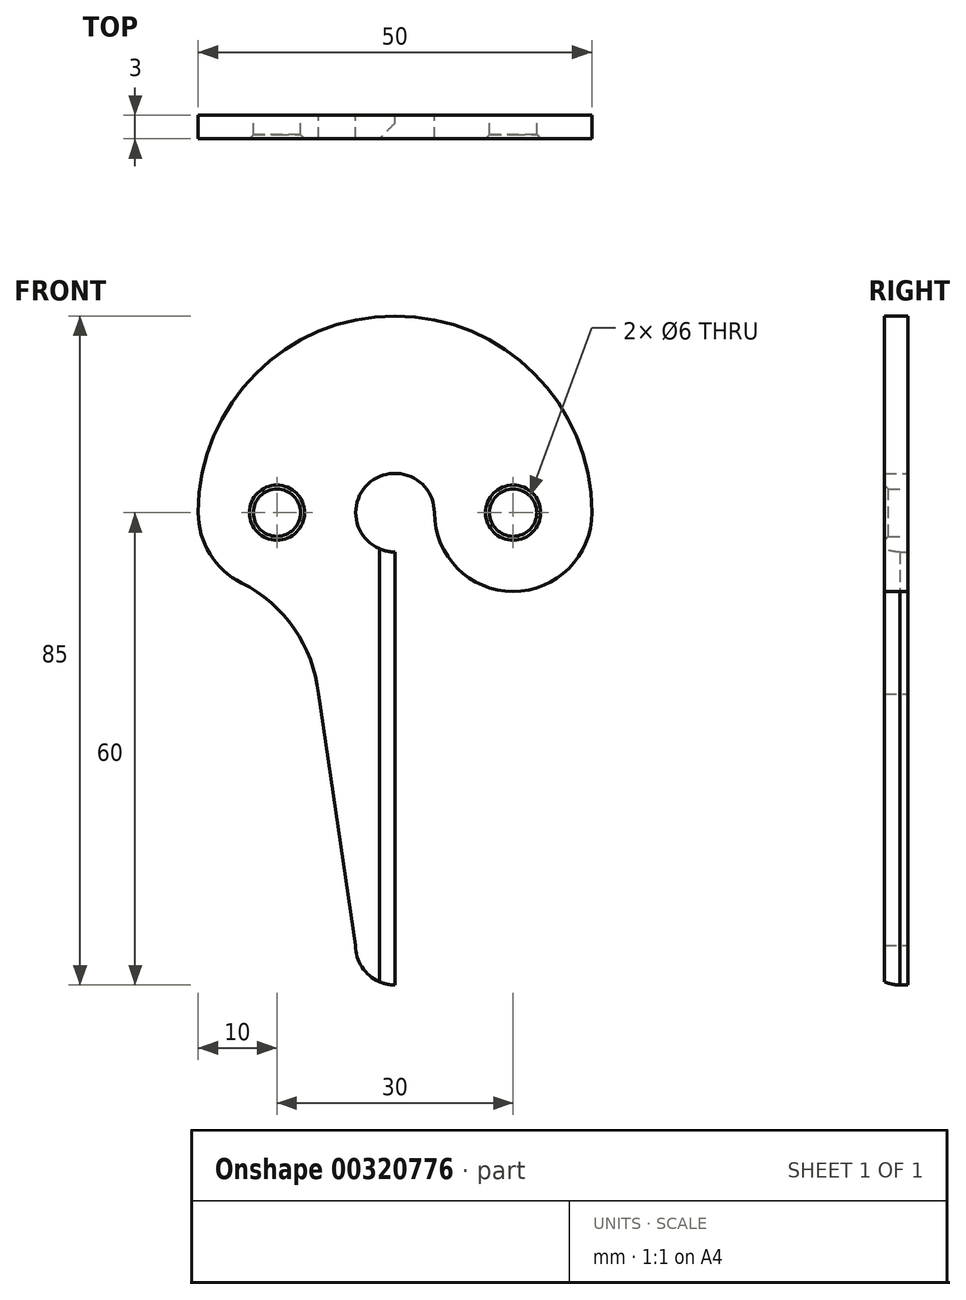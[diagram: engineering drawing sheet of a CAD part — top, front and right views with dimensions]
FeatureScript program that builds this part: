
annotation { "Feature Type Name" : "Feature", "Feature Type Description" : "" }
export const myFeature = defineFeature(function(context is Context, id is Id, definition is map)
    precondition{}
    {
        {
            var Q0;
            Q0=qCreatedBy(makeId("Front.planeOp"),FACE);
            var sketch = newSketch(context, id + "F0", { "sketchPlane" : qUnion([Q0])});
            skArc(sketch, "E0", {"start": v(25, 0) * mm, "mid": v(0, 25) * mm, "end": v(-25, 0) * mm});
            skArc(sketch, "E1", {"start": v(5, 0) * mm, "mid": v(-3.54, 3.54) * mm, "end": v(0, -5) * mm});
            skCircle(sketch, "E2", {"center": v(-15, 0) * mm, "radius": 3 * mm});
            skCircle(sketch, "E3", {"center": v(15, 0) * mm, "radius": 3 * mm});
            skCircle(sketch, "E4", {"center": v(-15, 0) * mm, "radius": 3.5 * mm});
            skCircle(sketch, "E5", {"center": v(15, 0) * mm, "radius": 3.5 * mm});
            skArc(sketch, "E6", {"start": v(-25, 0) * mm, "mid": v(-15, -10) * mm, "end": v(-5, 0) * mm});
            skArc(sketch, "E7", {"start": v(5, 0) * mm, "mid": v(15, -10) * mm, "end": v(25, 0) * mm});
            skPoint(sketch, "E8", {"position": v(-27.6, -25) * mm});
            skPoint(sketch, "E9", {"position": v(27.6, -25) * mm});
            skPoint(sketch, "E10", {"position": v(0, -54.97) * mm});
            skArc(sketch, "E11", {"start": v(-5.03, -54.97) * mm, "mid": v(-3.56, -58.53) * mm, "end": v(0, -60) * mm});
            skArc(sketch, "E12", {"start": v(-9.72, -23.03) * mm, "mid": v(-12.82, -14.74) * mm, "end": v(-19.5, -8.93) * mm});
            skLineSegment(sketch, "E13", {"start": v(-5.03, -54.97) * mm, "end": v(-9.72, -23.03) * mm});
            skPoint(sketch, "E14", {"position": v(0, -5) * mm});
            skLineSegment(sketch, "E15", {"start": v(0, -5) * mm, "end": v(0, -60) * mm});
            skLineSegment(sketch, "E16", {"start": v(-2, -4.58) * mm, "end": v(-2, -60) * mm});
            skSolve(sketch);
        }
        {
            var Q0;
            Q0 = qSketchRegion(id + "F0", true);
            var Q1;
            Q1=makeQuery(id+"F0.imprint","IMPRINT",FACE,{"disambiguationData":[TD([[makeQuery(id+"F0.imprint","IMPRINT",EDGE,{"derivedFrom":sQuery(id+"F0.wireOp",EDGE,"E2")}),-1.0]])]});
            var Q2;
            Q2=makeQuery(id+"F0.imprint","IMPRINT",FACE,{"disambiguationData":[TD([[makeQuery(id+"F0.imprint","IMPRINT",EDGE,{"derivedFrom":sQuery(id+"F0.wireOp",EDGE,"E3")}),-1.0]])]});
            extrude(context, id + "F1", {"entities" : qUnion([Q0, Q1, Q2]), "depth" : 3 * mm});
        }
        {
            var Q0;
            Q0=makeQuery(id+"F1.opExtrude","CAP_EDGE",EDGE,{"disambiguationData":[OSD([sQuery(id+"F0.wireOp",EDGE,"E2")])],"isStart":false});
            var Q1;
            Q1=makeQuery(id+"F1.opExtrude","CAP_EDGE",EDGE,{"disambiguationData":[OSD([sQuery(id+"F0.wireOp",EDGE,"E3")])],"isStart":false});
            chamfer(context, id + "F2", {"entities" : qUnion([Q0, Q1]), "width" : 0.5 * mm, "tangentPropagation" : true});
        }
        {
            var Q0;
            Q0=makeQuery(id+"F1.opExtrude","CAP_EDGE",EDGE,{"disambiguationData":[OSD([sQuery(id+"F0.wireOp",EDGE,"E15")])],"isStart":false});
            chamfer(context, id + "F3", {"entities" : qUnion([Q0]), "width" : 2 * mm, "tangentPropagation" : true});
        }
    });
